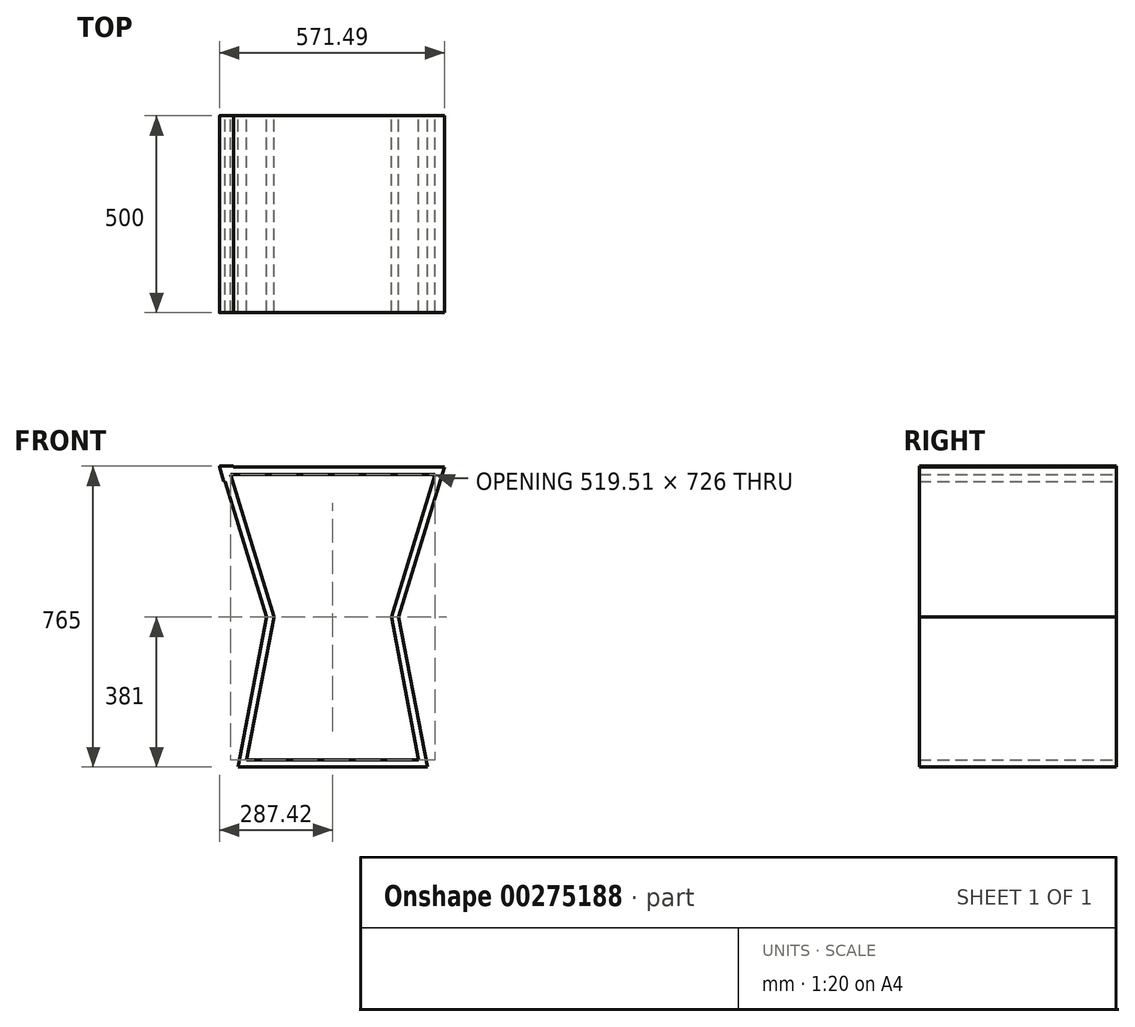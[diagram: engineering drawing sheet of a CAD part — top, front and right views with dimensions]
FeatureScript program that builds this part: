
annotation { "Feature Type Name" : "Feature", "Feature Type Description" : "" }
export const myFeature = defineFeature(function(context is Context, id is Id, definition is map)
    precondition{}
    {
        {
            var Q0;
            Q0=qCreatedBy(makeId("Front.planeOp"),FACE);
            var sketch = newSketch(context, id + "F0", { "sketchPlane" : qUnion([Q0])});
            skLineSegment(sketch, "E0", {"start": v(-284.07, 381) * mm, "end": v(-167.83, 0) * mm});
            skLineSegment(sketch, "E1", {"start": v(-167.83, 0) * mm, "end": v(-240.61, -381) * mm});
            skLineSegment(sketch, "E2", {"start": v(-240.61, -381) * mm, "end": v(240.61, -381) * mm});
            skLineSegment(sketch, "E3", {"start": v(240.61, -381) * mm, "end": v(167.83, 0) * mm});
            skLineSegment(sketch, "E4", {"start": v(167.83, 0) * mm, "end": v(284.07, 381) * mm});
            skLineSegment(sketch, "E5", {"start": v(284.07, 381) * mm, "end": v(-284.07, 381) * mm});
            skLineSegment(sketch, "E6", {"start": v(0, 381) * mm, "end": v(0, -381) * mm, "construction": true});
            skLineSegment(sketch, "E7", {"start": v(-167.83, 0) * mm, "end": v(167.83, 0) * mm, "construction": true});
            skLineSegment(sketch, "E8.0", {"start": v(149.31, 1) * mm, "end": v(259.76, 363) * mm});
            skLineSegment(sketch, "E8.1", {"start": v(-259.76, 363) * mm, "end": v(-149.31, 1) * mm});
            skLineSegment(sketch, "E8.2", {"start": v(-149.31, 1) * mm, "end": v(-218.85, -363) * mm});
            skLineSegment(sketch, "E8.3", {"start": v(259.76, 363) * mm, "end": v(-259.76, 363) * mm});
            skLineSegment(sketch, "E8.4", {"start": v(-218.85, -363) * mm, "end": v(218.85, -363) * mm});
            skLineSegment(sketch, "E8.5", {"start": v(218.85, -363) * mm, "end": v(149.31, 1) * mm});
            skLineSegment(sketch, "E9", {"start": v(-259.76, 363) * mm, "end": v(-278.57, 363) * mm});
            skLineSegment(sketch, "E10", {"start": v(-273.04, 344.85) * mm, "end": v(-274, 344.55) * mm});
            skLineSegment(sketch, "E11", {"start": v(-276.49, 345.88) * mm, "end": v(-287.33, 381.42) * mm});
            skLineSegment(sketch, "E12", {"start": v(-285.42, 384) * mm, "end": v(-254.22, 384) * mm});
            skLineSegment(sketch, "E13", {"start": v(-252.22, 382) * mm, "end": v(-252.22, 381) * mm});
            skLineSegment(sketch, "E14", {"start": v(-284.07, 381) * mm, "end": v(-287.2, 381) * mm});
            skPoint(sketch, "E15.visualSharp", {"position": v(-288.12, 384) * mm});
            skArc(sketch, "E15.filletArc", {"start": v(-285.42, 384) * mm, "mid": v(-287.02, 383.2) * mm, "end": v(-287.33, 381.42) * mm});
            skPoint(sketch, "E16.visualSharp", {"position": v(-252.22, 384) * mm});
            skArc(sketch, "E16.filletArc", {"start": v(-252.22, 382) * mm, "mid": v(-252.8, 383.41) * mm, "end": v(-254.22, 384) * mm});
            skPoint(sketch, "E17.visualSharp", {"position": v(-275.9, 343.97) * mm});
            skArc(sketch, "E17.filletArc", {"start": v(-276.49, 345.88) * mm, "mid": v(-275.52, 344.7) * mm, "end": v(-274, 344.55) * mm});
            skSolve(sketch);
        }
        {
            var Q0;
            {var subQ7=sQuery(id+"F0.wireOp",EDGE,"E1");Q0=makeQuery(id+"F0.imprint","IMPRINT",FACE,{"disambiguationData":[TD([[makeQuery(id+"F0.imprint","IMPRINT",EDGE,{"derivedFrom":subQ7}),1.0]])]});}
            var Q1;
            Q1=makeQuery(id+"F0.imprint","IMPRINT",FACE,{"disambiguationData":[TD([[makeQuery(id+"F0.imprint","IMPRINT",EDGE,{"derivedFrom":sQuery(id+"F0.wireOp",EDGE,"E12")}),-1.0]])]});
            var Q2;
            {var subQ5=sQuery(id+"F0.wireOp",EDGE,"E10");Q2=makeQuery(id+"F0.imprint","IMPRINT",FACE,{"disambiguationData":[TD([[makeQuery(id+"F0.imprint","IMPRINT",EDGE,{"derivedFrom":subQ5}),-1.0]])]});}
            extrude(context, id + "F1", {"entities" : qUnion([Q0, Q1, Q2]), "depth" : 500 * mm, "offsetDistance" : 25 * mm});
        }
    });
